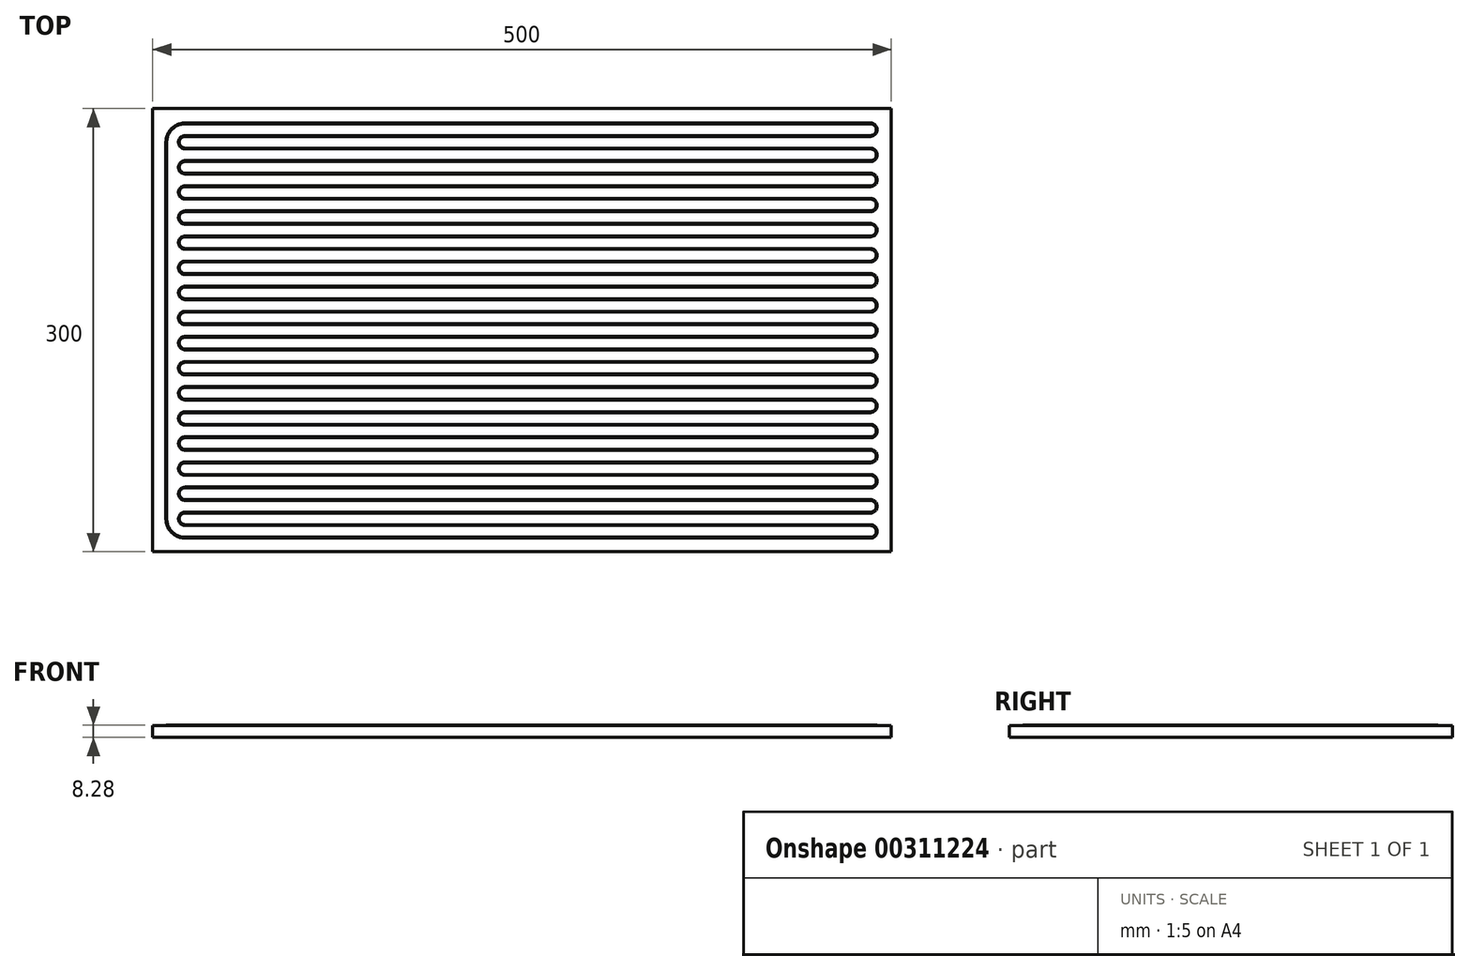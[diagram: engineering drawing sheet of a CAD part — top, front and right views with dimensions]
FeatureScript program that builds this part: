
annotation { "Feature Type Name" : "Feature", "Feature Type Description" : "" }
export const myFeature = defineFeature(function(context is Context, id is Id, definition is map)
    precondition{}
    {
        {
            var Q0;
            Q0=qCreatedBy(makeId("Top.planeOp"),FACE);
            var sketch = newSketch(context, id + "F0", { "sketchPlane" : qUnion([Q0])});
            skLineSegment(sketch, "E0.bottom", {"start": v(-246.57, -213.11) * mm, "end": v(253.43, -213.11) * mm});
            skLineSegment(sketch, "E0.top", {"start": v(-246.57, 86.89) * mm, "end": v(253.43, 86.89) * mm});
            skLineSegment(sketch, "E0.left", {"start": v(-246.57, -213.11) * mm, "end": v(-246.57, 86.89) * mm});
            skLineSegment(sketch, "E0.right", {"start": v(253.43, -213.11) * mm, "end": v(253.43, 86.89) * mm});
            skSolve(sketch);
        }
        {
            var Q0;
            Q0=makeQuery(id+"F0.imprint","IMPRINT",FACE,{"disambiguationData":[TD([[makeQuery(id+"F0.imprint","IMPRINT",EDGE,{"derivedFrom":sQuery(id+"F0.wireOp",EDGE,"E0.bottom")}),1.0]])]});
            extrude(context, id + "F1", {"entities" : qUnion([Q0]), "depth" : 8 * mm});
        }
        {
            var Q0;
            Q0=makeQuery(id+"F1.opExtrude","CAP_FACE",FACE,{"disambiguationData":[OSD([sQuery(id+"F0.wireOp",EDGE,"E0.bottom"),sQuery(id+"F0.wireOp",EDGE,"E0.top"),sQuery(id+"F0.wireOp",EDGE,"E0.left"),sQuery(id+"F0.wireOp",EDGE,"E0.right")])],"isStart":false});
            cPlane(context, id + "F2", {"entities" : qUnion([Q0]), "cplaneType" : CPlaneType.OFFSET, "offset" : 1 * mm, "width" : 150 * mm, "height" : 150 * mm});
        }
        {
            var Q0;
            Q0=makeQuery(id+"F1.opExtrude","CAP_FACE",FACE,{"disambiguationData":[OSD([sQuery(id+"F0.wireOp",EDGE,"E0.bottom"),sQuery(id+"F0.wireOp",EDGE,"E0.top"),sQuery(id+"F0.wireOp",EDGE,"E0.left"),sQuery(id+"F0.wireOp",EDGE,"E0.right")])],"isStart":false});
            var sketch = newSketch(context, id + "F3", { "sketchPlane" : qUnion([Q0])});
            skLineSegment(sketch, "E1.0", {"start": v(-239.57, 79.89) * mm, "end": v(246.43, 79.89) * mm});
            skLineSegment(sketch, "E1.1", {"start": v(-239.57, -206.11) * mm, "end": v(-239.57, 79.89) * mm});
            skLineSegment(sketch, "E1.2", {"start": v(-239.57, -206.11) * mm, "end": v(246.43, -206.11) * mm});
            skLineSegment(sketch, "E1.3", {"start": v(246.43, -206.11) * mm, "end": v(246.43, 79.89) * mm});
            skSolve(sketch);
        }
        {
            var Q0;
            Q0=makeQuery(id+"F1.opExtrude","SWEPT_BODY",BODY,{"disambiguationData":[OSD([sQuery(id+"F0.wireOp",EDGE,"E0.bottom"),sQuery(id+"F0.wireOp",EDGE,"E0.top"),sQuery(id+"F0.wireOp",EDGE,"E0.left"),sQuery(id+"F0.wireOp",EDGE,"E0.right")])]});
            var Q1;
            Q1=makeQuery(id+"F3.imprint","IMPRINT",FACE,{"disambiguationData":[TD([[makeQuery(id+"F3.imprint","IMPRINT",EDGE,{"derivedFrom":sQuery(id+"F3.wireOp",EDGE,"E1.0")}),1.0]])]});
            transform(context, id + "F4", {"entities" : qUnion([Q0]), "transformType" : TransformType.TRANSLATION_DISTANCE, "transformDirection" : qUnion([Q1]), "distance" : 1 * mm, "makeCopy" : false});
        }
        {
            var Q0;
            Q0=qCreatedBy(id+"F2.planeOp",FACE);
            var sketch = newSketch(context, id + "F5", { "sketchPlane" : qUnion([Q0])});
            skLineSegment(sketch, "E2", {"start": v(-224.57, -203.61) * mm, "end": v(239.43, -203.61) * mm});
            skLineSegment(sketch, "E3", {"start": v(-224.57, -195.11) * mm, "end": v(239.43, -195.11) * mm});
            skArc(sketch, "E4", {"start": v(239.43, -195.11) * mm, "mid": v(243.68, -199.36) * mm, "end": v(239.43, -203.61) * mm});
            skArc(sketch, "E5", {"start": v(-224.57, -195.11) * mm, "mid": v(-228.82, -190.86) * mm, "end": v(-224.57, -186.61) * mm});
            skLineSegment(sketch, "E6.0.1.0", {"start": v(-224.57, -186.61) * mm, "end": v(239.43, -186.61) * mm});
            skLineSegment(sketch, "E6.0.1.1", {"start": v(-224.57, -178.11) * mm, "end": v(239.43, -178.11) * mm});
            skArc(sketch, "E6.0.1.2", {"start": v(-224.57, -178.11) * mm, "mid": v(-228.82, -173.86) * mm, "end": v(-224.57, -169.61) * mm});
            skArc(sketch, "E6.0.1.3", {"start": v(239.43, -178.11) * mm, "mid": v(243.68, -182.36) * mm, "end": v(239.43, -186.61) * mm});
            skLineSegment(sketch, "E6.0.2.0", {"start": v(-224.57, -169.61) * mm, "end": v(239.43, -169.61) * mm});
            skLineSegment(sketch, "E6.0.2.1", {"start": v(-224.57, -161.11) * mm, "end": v(239.43, -161.11) * mm});
            skArc(sketch, "E6.0.2.2", {"start": v(-224.57, -161.11) * mm, "mid": v(-228.82, -156.86) * mm, "end": v(-224.57, -152.61) * mm});
            skArc(sketch, "E6.0.2.3", {"start": v(239.43, -161.11) * mm, "mid": v(243.68, -165.36) * mm, "end": v(239.43, -169.61) * mm});
            skLineSegment(sketch, "E6.0.3.0", {"start": v(-224.57, -152.61) * mm, "end": v(239.43, -152.61) * mm});
            skLineSegment(sketch, "E6.0.3.1", {"start": v(-224.57, -144.11) * mm, "end": v(239.43, -144.11) * mm});
            skArc(sketch, "E6.0.3.2", {"start": v(-224.57, -144.11) * mm, "mid": v(-228.82, -139.86) * mm, "end": v(-224.57, -135.61) * mm});
            skArc(sketch, "E6.0.3.3", {"start": v(239.43, -144.11) * mm, "mid": v(243.68, -148.36) * mm, "end": v(239.43, -152.61) * mm});
            skLineSegment(sketch, "E6.0.4.0", {"start": v(-224.57, -135.61) * mm, "end": v(239.43, -135.61) * mm});
            skLineSegment(sketch, "E6.0.4.1", {"start": v(-224.57, -127.11) * mm, "end": v(239.43, -127.11) * mm});
            skArc(sketch, "E6.0.4.2", {"start": v(-224.57, -127.11) * mm, "mid": v(-228.82, -122.86) * mm, "end": v(-224.57, -118.61) * mm});
            skArc(sketch, "E6.0.4.3", {"start": v(239.43, -127.11) * mm, "mid": v(243.68, -131.36) * mm, "end": v(239.43, -135.61) * mm});
            skLineSegment(sketch, "E6.direction1", {"start": v(-224.57, -203.61) * mm, "end": v(-206.57, -203.61) * mm, "construction": true});
            skLineSegment(sketch, "E6.direction2", {"start": v(-224.57, -203.61) * mm, "end": v(-224.57, -186.61) * mm, "construction": true});
            skLineSegment(sketch, "E7.0.0.5", {"start": v(-224.57, -118.61) * mm, "end": v(239.43, -118.61) * mm});
            skLineSegment(sketch, "E7.3.0.5", {"start": v(-224.57, -110.11) * mm, "end": v(239.43, -110.11) * mm});
            skArc(sketch, "E7.6.0.5", {"start": v(-224.57, -110.11) * mm, "mid": v(-228.82, -105.86) * mm, "end": v(-224.57, -101.61) * mm});
            skArc(sketch, "E7.10.0.5", {"start": v(239.43, -110.11) * mm, "mid": v(243.68, -114.36) * mm, "end": v(239.43, -118.61) * mm});
            skLineSegment(sketch, "E7.0.0.6", {"start": v(-224.57, -101.61) * mm, "end": v(239.43, -101.61) * mm});
            skLineSegment(sketch, "E7.3.0.6", {"start": v(-224.57, -93.11) * mm, "end": v(239.43, -93.11) * mm});
            skArc(sketch, "E7.6.0.6", {"start": v(-224.57, -93.11) * mm, "mid": v(-228.82, -88.86) * mm, "end": v(-224.57, -84.61) * mm});
            skArc(sketch, "E7.10.0.6", {"start": v(239.43, -93.11) * mm, "mid": v(243.68, -97.36) * mm, "end": v(239.43, -101.61) * mm});
            skLineSegment(sketch, "E7.0.0.7", {"start": v(-224.57, -84.61) * mm, "end": v(239.43, -84.61) * mm});
            skLineSegment(sketch, "E7.3.0.7", {"start": v(-224.57, -76.11) * mm, "end": v(239.43, -76.11) * mm});
            skArc(sketch, "E7.6.0.7", {"start": v(-224.57, -76.11) * mm, "mid": v(-228.82, -71.86) * mm, "end": v(-224.57, -67.61) * mm});
            skArc(sketch, "E7.10.0.7", {"start": v(239.43, -76.11) * mm, "mid": v(243.68, -80.36) * mm, "end": v(239.43, -84.61) * mm});
            skLineSegment(sketch, "E7.0.0.8", {"start": v(-224.57, -67.61) * mm, "end": v(239.43, -67.61) * mm});
            skLineSegment(sketch, "E7.3.0.8", {"start": v(-224.57, -59.11) * mm, "end": v(239.43, -59.11) * mm});
            skArc(sketch, "E7.6.0.8", {"start": v(-224.57, -59.11) * mm, "mid": v(-228.82, -54.86) * mm, "end": v(-224.57, -50.61) * mm});
            skArc(sketch, "E7.10.0.8", {"start": v(239.43, -59.11) * mm, "mid": v(243.68, -63.36) * mm, "end": v(239.43, -67.61) * mm});
            skLineSegment(sketch, "E7.0.0.9", {"start": v(-224.57, -50.61) * mm, "end": v(239.43, -50.61) * mm});
            skLineSegment(sketch, "E7.3.0.9", {"start": v(-224.57, -42.11) * mm, "end": v(239.43, -42.11) * mm});
            skArc(sketch, "E7.6.0.9", {"start": v(-224.57, -42.11) * mm, "mid": v(-228.82, -37.86) * mm, "end": v(-224.57, -33.61) * mm});
            skArc(sketch, "E7.10.0.9", {"start": v(239.43, -42.11) * mm, "mid": v(243.68, -46.36) * mm, "end": v(239.43, -50.61) * mm});
            skLineSegment(sketch, "E8.0.0.10", {"start": v(-224.57, -33.61) * mm, "end": v(239.43, -33.61) * mm});
            skLineSegment(sketch, "E8.3.0.10", {"start": v(-224.57, -25.11) * mm, "end": v(239.43, -25.11) * mm});
            skArc(sketch, "E8.6.0.10", {"start": v(-224.57, -25.11) * mm, "mid": v(-228.82, -20.86) * mm, "end": v(-224.57, -16.61) * mm});
            skArc(sketch, "E8.10.0.10", {"start": v(239.43, -25.11) * mm, "mid": v(243.68, -29.36) * mm, "end": v(239.43, -33.61) * mm});
            skLineSegment(sketch, "E9.0.0.11", {"start": v(-224.57, -16.61) * mm, "end": v(239.43, -16.61) * mm});
            skLineSegment(sketch, "E9.3.0.11", {"start": v(-224.57, -8.11) * mm, "end": v(239.43, -8.11) * mm});
            skArc(sketch, "E9.6.0.11", {"start": v(-224.57, -8.11) * mm, "mid": v(-228.82, -3.86) * mm, "end": v(-224.57, 0.39) * mm});
            skArc(sketch, "E9.10.0.11", {"start": v(239.43, -8.11) * mm, "mid": v(243.68, -12.36) * mm, "end": v(239.43, -16.61) * mm});
            skLineSegment(sketch, "E10.0.0.12", {"start": v(-224.57, 0.39) * mm, "end": v(239.43, 0.39) * mm});
            skLineSegment(sketch, "E10.3.0.12", {"start": v(-224.57, 8.89) * mm, "end": v(239.43, 8.89) * mm});
            skArc(sketch, "E10.6.0.12", {"start": v(-224.57, 8.89) * mm, "mid": v(-228.82, 13.14) * mm, "end": v(-224.57, 17.39) * mm});
            skArc(sketch, "E10.10.0.12", {"start": v(239.43, 8.89) * mm, "mid": v(243.68, 4.64) * mm, "end": v(239.43, 0.39) * mm});
            skLineSegment(sketch, "E11.0.0.13", {"start": v(-224.57, 17.39) * mm, "end": v(239.43, 17.39) * mm});
            skLineSegment(sketch, "E11.3.0.13", {"start": v(-224.57, 25.89) * mm, "end": v(239.43, 25.89) * mm});
            skArc(sketch, "E11.6.0.13", {"start": v(-224.57, 25.89) * mm, "mid": v(-228.82, 30.14) * mm, "end": v(-224.57, 34.39) * mm});
            skArc(sketch, "E11.10.0.13", {"start": v(239.43, 25.89) * mm, "mid": v(243.68, 21.64) * mm, "end": v(239.43, 17.39) * mm});
            skLineSegment(sketch, "E12.0.0.14", {"start": v(-224.57, 34.39) * mm, "end": v(239.43, 34.39) * mm});
            skLineSegment(sketch, "E12.3.0.14", {"start": v(-224.57, 42.89) * mm, "end": v(239.43, 42.89) * mm});
            skArc(sketch, "E12.6.0.14", {"start": v(-224.57, 42.89) * mm, "mid": v(-228.82, 47.14) * mm, "end": v(-224.57, 51.39) * mm});
            skArc(sketch, "E12.10.0.14", {"start": v(239.43, 42.89) * mm, "mid": v(243.68, 38.64) * mm, "end": v(239.43, 34.39) * mm});
            skLineSegment(sketch, "E13.0.0.15", {"start": v(-224.57, 51.39) * mm, "end": v(239.43, 51.39) * mm});
            skLineSegment(sketch, "E13.3.0.15", {"start": v(-224.57, 59.89) * mm, "end": v(239.43, 59.89) * mm});
            skArc(sketch, "E13.6.0.15", {"start": v(-224.57, 59.89) * mm, "mid": v(-228.82, 64.14) * mm, "end": v(-224.57, 68.39) * mm});
            skArc(sketch, "E13.10.0.15", {"start": v(239.43, 59.89) * mm, "mid": v(243.68, 55.64) * mm, "end": v(239.43, 51.39) * mm});
            skLineSegment(sketch, "E14.0.0.16", {"start": v(-224.57, 68.39) * mm, "end": v(239.43, 68.39) * mm});
            skLineSegment(sketch, "E14.3.0.16", {"start": v(-224.57, 76.89) * mm, "end": v(239.43, 76.89) * mm});
            skArc(sketch, "E14.10.0.16", {"start": v(239.43, 76.89) * mm, "mid": v(243.68, 72.64) * mm, "end": v(239.43, 68.39) * mm});
            skArc(sketch, "E15", {"start": v(-224.57, -203.61) * mm, "mid": v(-233.59, -199.88) * mm, "end": v(-237.32, -190.86) * mm});
            skArc(sketch, "E16", {"start": v(-224.57, 76.89) * mm, "mid": v(-233.59, 73.16) * mm, "end": v(-237.32, 64.14) * mm});
            skLineSegment(sketch, "E17", {"start": v(-237.32, 64.14) * mm, "end": v(-237.32, -190.86) * mm});
            skSolve(sketch);
        }
        {
            var Q0;
            Q0=qCreatedBy(makeId("Right.planeOp"),FACE);
            var sketch = newSketch(context, id + "F6", { "sketchPlane" : qUnion([Q0])});
            skLineSegment(sketch, "E18", {"start": v(59.89, 9) * mm, "end": v(51.39, 9) * mm});
            skLineSegment(sketch, "E19", {"start": v(42.89, 9) * mm, "end": v(34.39, 9) * mm});
            skLineSegment(sketch, "E20", {"start": v(25.89, 9) * mm, "end": v(17.39, 9) * mm});
            skLineSegment(sketch, "E21", {"start": v(8.89, 9) * mm, "end": v(0.39, 9) * mm});
            skLineSegment(sketch, "E22", {"start": v(-8.11, 9) * mm, "end": v(-16.61, 9) * mm});
            skLineSegment(sketch, "E23", {"start": v(-25.11, 9) * mm, "end": v(-33.61, 9) * mm});
            skLineSegment(sketch, "E24", {"start": v(-42.11, 9) * mm, "end": v(-50.61, 9) * mm});
            skLineSegment(sketch, "E25", {"start": v(-59.11, 9) * mm, "end": v(-67.61, 9) * mm});
            skLineSegment(sketch, "E26", {"start": v(-76.11, 9) * mm, "end": v(-84.61, 9) * mm});
            skLineSegment(sketch, "E27", {"start": v(-93.11, 9) * mm, "end": v(-101.61, 9) * mm});
            skLineSegment(sketch, "E28", {"start": v(-110.11, 9) * mm, "end": v(-118.61, 9) * mm});
            skLineSegment(sketch, "E29", {"start": v(-127.11, 9) * mm, "end": v(-135.61, 9) * mm});
            skLineSegment(sketch, "E30", {"start": v(-144.11, 9) * mm, "end": v(-152.61, 9) * mm});
            skLineSegment(sketch, "E31", {"start": v(-161.11, 9) * mm, "end": v(-169.61, 9) * mm});
            skLineSegment(sketch, "E32", {"start": v(-178.11, 9) * mm, "end": v(-186.61, 9) * mm});
            skLineSegment(sketch, "E33", {"start": v(-195.11, 9) * mm, "end": v(-203.61, 9) * mm});
            skLineSegment(sketch, "E34", {"start": v(76.89, 9) * mm, "end": v(68.39, 9) * mm});
            skCircle(sketch, "E35", {"center": v(-203.61, 9) * mm, "radius": 0.28 * mm});
            skSolve(sketch);
        }
        {
            var Q0;
            Q0=makeQuery(id+"F6.imprint","IMPRINT",FACE,{"disambiguationData":[TD([[makeQuery(id+"F6.imprint","IMPRINT",EDGE,{"derivedFrom":sQuery(id+"F6.wireOp",EDGE,"E35")}),1.0]])]});
            var Q1;
            Q1=sQuery(id+"F5.wireOp",EDGE,"E2");
            var Q2;
            Q2=sQuery(id+"F5.wireOp",EDGE,"E15");
            var Q3;
            Q3=sQuery(id+"F5.wireOp",EDGE,"E3");
            var Q4;
            Q4=sQuery(id+"F5.wireOp",EDGE,"E17");
            var Q5;
            Q5=sQuery(id+"F5.wireOp",EDGE,"E5");
            var Q6;
            Q6=sQuery(id+"F5.wireOp",EDGE,"E6.0.1.0");
            var Q7;
            Q7=sQuery(id+"F5.wireOp",EDGE,"E6.0.1.2");
            var Q8;
            Q8=sQuery(id+"F5.wireOp",EDGE,"E6.0.2.2");
            var Q9;
            Q9=sQuery(id+"F5.wireOp",EDGE,"E6.0.3.2");
            var Q10;
            Q10=sQuery(id+"F5.wireOp",EDGE,"E6.0.2.0");
            var Q11;
            Q11=sQuery(id+"F5.wireOp",EDGE,"E6.0.1.1");
            var Q12;
            Q12=sQuery(id+"F5.wireOp",EDGE,"E6.0.3.0");
            var Q13;
            Q13=sQuery(id+"F5.wireOp",EDGE,"E6.0.3.1");
            var Q14;
            Q14=sQuery(id+"F5.wireOp",EDGE,"E6.0.2.1");
            var Q15;
            Q15=sQuery(id+"F5.wireOp",EDGE,"E4");
            var Q16;
            Q16=sQuery(id+"F5.wireOp",EDGE,"E6.0.1.3");
            var Q17;
            Q17=sQuery(id+"F5.wireOp",EDGE,"E6.0.2.3");
            var Q18;
            Q18=sQuery(id+"F5.wireOp",EDGE,"E6.0.3.3");
            var Q19;
            Q19=sQuery(id+"F5.wireOp",EDGE,"E16");
            var Q20;
            Q20=sQuery(id+"F5.wireOp",EDGE,"E14.3.0.16");
            var Q21;
            Q21=sQuery(id+"F5.wireOp",EDGE,"E13.6.0.15");
            var Q22;
            Q22=sQuery(id+"F5.wireOp",EDGE,"E12.6.0.14");
            var Q23;
            Q23=sQuery(id+"F5.wireOp",EDGE,"E11.6.0.13");
            var Q24;
            Q24=sQuery(id+"F5.wireOp",EDGE,"E10.6.0.12");
            var Q25;
            Q25=sQuery(id+"F5.wireOp",EDGE,"E9.6.0.11");
            var Q26;
            Q26=sQuery(id+"F5.wireOp",EDGE,"E8.6.0.10");
            var Q27;
            Q27=sQuery(id+"F5.wireOp",EDGE,"E7.6.0.9");
            var Q28;
            Q28=sQuery(id+"F5.wireOp",EDGE,"E7.6.0.8");
            var Q29;
            Q29=sQuery(id+"F5.wireOp",EDGE,"E7.6.0.7");
            var Q30;
            Q30=sQuery(id+"F5.wireOp",EDGE,"E7.6.0.6");
            var Q31;
            Q31=sQuery(id+"F5.wireOp",EDGE,"E7.6.0.5");
            var Q32;
            Q32=sQuery(id+"F5.wireOp",EDGE,"E6.0.4.2");
            var Q33;
            Q33=sQuery(id+"F5.wireOp",EDGE,"E6.0.4.0");
            var Q34;
            Q34=sQuery(id+"F5.wireOp",EDGE,"E6.0.4.1");
            var Q35;
            Q35=sQuery(id+"F5.wireOp",EDGE,"E7.0.0.5");
            var Q36;
            Q36=sQuery(id+"F5.wireOp",EDGE,"E7.3.0.5");
            var Q37;
            Q37=sQuery(id+"F5.wireOp",EDGE,"E7.0.0.6");
            var Q38;
            Q38=sQuery(id+"F5.wireOp",EDGE,"E7.3.0.6");
            var Q39;
            Q39=sQuery(id+"F5.wireOp",EDGE,"E7.0.0.7");
            var Q40;
            Q40=sQuery(id+"F5.wireOp",EDGE,"E7.3.0.7");
            var Q41;
            Q41=sQuery(id+"F5.wireOp",EDGE,"E7.0.0.8");
            var Q42;
            Q42=sQuery(id+"F5.wireOp",EDGE,"E7.3.0.8");
            var Q43;
            Q43=sQuery(id+"F5.wireOp",EDGE,"E7.0.0.9");
            var Q44;
            Q44=sQuery(id+"F5.wireOp",EDGE,"E7.3.0.9");
            var Q45;
            Q45=sQuery(id+"F5.wireOp",EDGE,"E8.0.0.10");
            var Q46;
            Q46=sQuery(id+"F5.wireOp",EDGE,"E8.3.0.10");
            var Q47;
            Q47=sQuery(id+"F5.wireOp",EDGE,"E9.0.0.11");
            var Q48;
            Q48=sQuery(id+"F5.wireOp",EDGE,"E9.3.0.11");
            var Q49;
            Q49=sQuery(id+"F5.wireOp",EDGE,"E10.0.0.12");
            var Q50;
            Q50=sQuery(id+"F5.wireOp",EDGE,"E10.3.0.12");
            var Q51;
            Q51=sQuery(id+"F5.wireOp",EDGE,"E11.0.0.13");
            var Q52;
            Q52=sQuery(id+"F5.wireOp",EDGE,"E11.3.0.13");
            var Q53;
            Q53=sQuery(id+"F5.wireOp",EDGE,"E13.0.0.15");
            var Q54;
            Q54=sQuery(id+"F5.wireOp",EDGE,"E12.0.0.14");
            var Q55;
            Q55=sQuery(id+"F5.wireOp",EDGE,"E12.3.0.14");
            var Q56;
            Q56=sQuery(id+"F5.wireOp",EDGE,"E13.3.0.15");
            var Q57;
            Q57=sQuery(id+"F5.wireOp",EDGE,"E14.0.0.16");
            var Q58;
            Q58=sQuery(id+"F5.wireOp",EDGE,"E14.10.0.16");
            var Q59;
            Q59=sQuery(id+"F5.wireOp",EDGE,"E13.10.0.15");
            var Q60;
            Q60=sQuery(id+"F5.wireOp",EDGE,"E11.10.0.13");
            var Q61;
            Q61=sQuery(id+"F5.wireOp",EDGE,"E10.10.0.12");
            var Q62;
            Q62=sQuery(id+"F5.wireOp",EDGE,"E12.10.0.14");
            var Q63;
            Q63=sQuery(id+"F5.wireOp",EDGE,"E9.10.0.11");
            var Q64;
            Q64=sQuery(id+"F5.wireOp",EDGE,"E8.10.0.10");
            var Q65;
            Q65=sQuery(id+"F5.wireOp",EDGE,"E7.10.0.9");
            var Q66;
            Q66=sQuery(id+"F5.wireOp",EDGE,"E7.10.0.8");
            var Q67;
            Q67=sQuery(id+"F5.wireOp",EDGE,"E6.0.4.3");
            var Q68;
            Q68=sQuery(id+"F5.wireOp",EDGE,"E7.10.0.5");
            var Q69;
            Q69=sQuery(id+"F5.wireOp",EDGE,"E7.10.0.6");
            var Q70;
            Q70=sQuery(id+"F5.wireOp",EDGE,"E7.10.0.7");
            sweep(context, id + "F7", {"profiles" : qUnion([Q0]), "path" : qUnion([Q1, Q2, Q3, Q4, Q5, Q6, Q7, Q8, Q9, Q10, Q11, Q12, Q13, Q14, Q15, Q16, Q17, Q18, Q19, Q20, Q21, Q22, Q23, Q24, Q25, Q26, Q27, Q28, Q29, Q30, Q31, Q32, Q33, Q34, Q35, Q36, Q37, Q38, Q39, Q40, Q41, Q42, Q43, Q44, Q45, Q46, Q47, Q48, Q49, Q50, Q51, Q52, Q53, Q54, Q55, Q56, Q57, Q58, Q59, Q60, Q61, Q62, Q63, Q64, Q65, Q66, Q67, Q68, Q69, Q70])});
        }
    });
